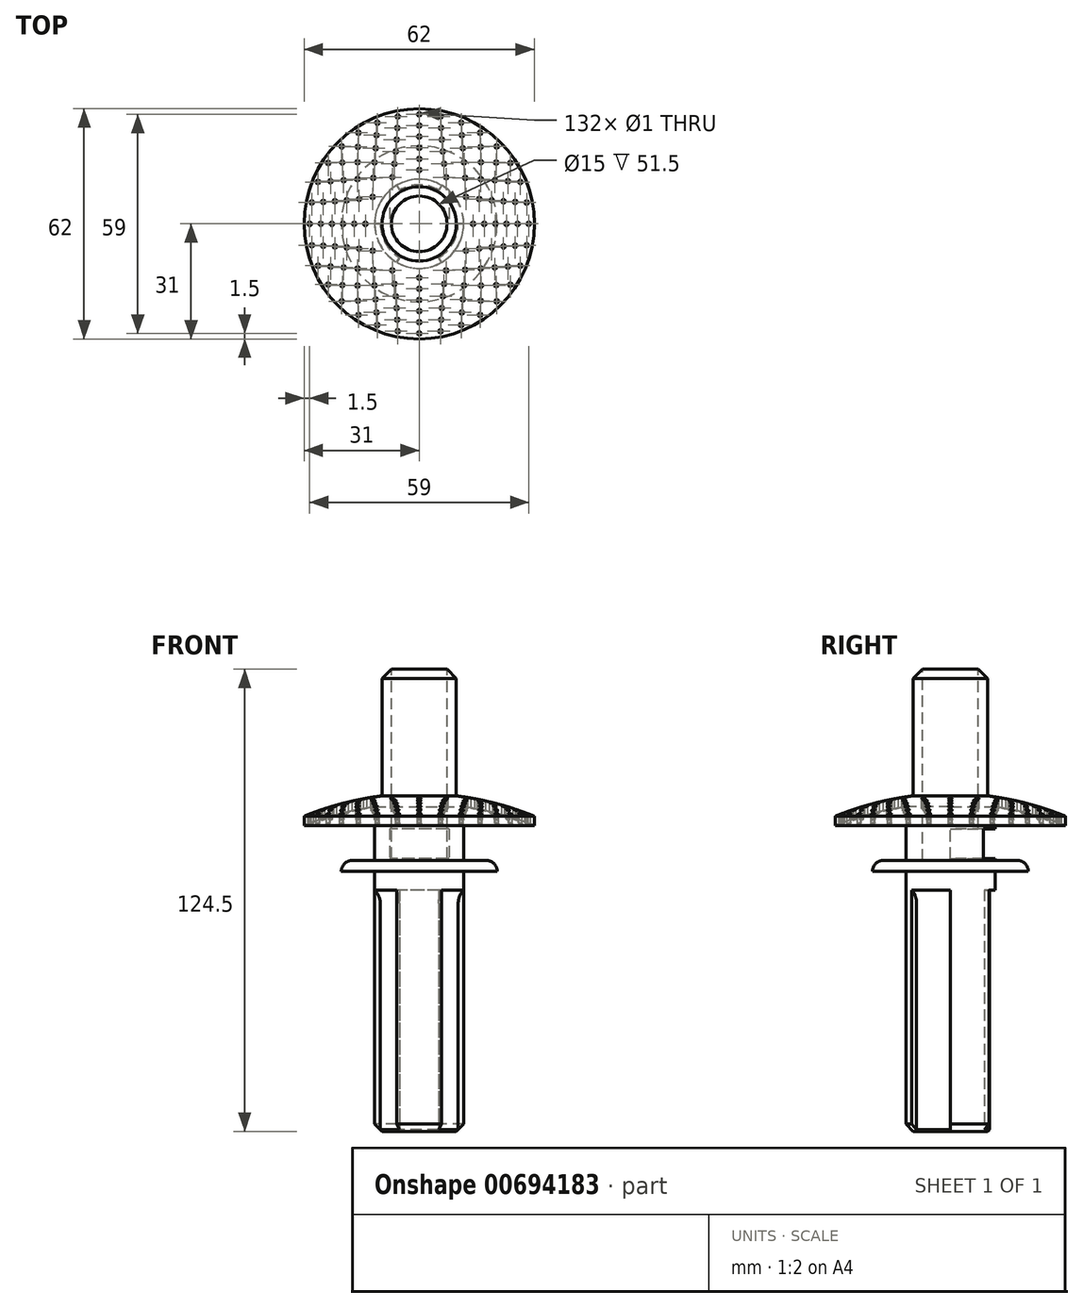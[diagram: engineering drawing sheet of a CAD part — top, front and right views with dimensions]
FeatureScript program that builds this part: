
annotation { "Feature Type Name" : "Feature", "Feature Type Description" : "" }
export const myFeature = defineFeature(function(context is Context, id is Id, definition is map)
    precondition{}
    {
        {
            var Q0;
            Q0=qCreatedBy(makeId("Top.planeOp"),FACE);
            var sketch = newSketch(context, id + "F0", { "sketchPlane" : qUnion([Q0])});
            skArc(sketch, "E0", {"start": v(-6, 10.4) * mm, "mid": v(-10.4, 6) * mm, "end": v(-12, 0) * mm});
            skArc(sketch, "E1", {"start": v(5.25, 9.1) * mm, "mid": v(0, 10.5) * mm, "end": v(-5.25, 9.1) * mm});
            skLineSegment(sketch, "E2", {"start": v(-5.25, 9.1) * mm, "end": v(-6, 10.4) * mm});
            skLineSegment(sketch, "E3", {"start": v(5.25, 9.1) * mm, "end": v(6, 10.4) * mm});
            skArc(sketch, "E4.1.0", {"start": v(-10.5, 0) * mm, "mid": v(-9.1, -5.25) * mm, "end": v(-5.25, -9.1) * mm});
            skArc(sketch, "E4.2.0", {"start": v(5.25, -9.1) * mm, "mid": v(9.1, -5.25) * mm, "end": v(10.5, 0) * mm});
            skLineSegment(sketch, "E5.1.0", {"start": v(-10.5, 0) * mm, "end": v(-12, 0) * mm});
            skLineSegment(sketch, "E5.1.1", {"start": v(-5.25, -9.1) * mm, "end": v(-6, -10.4) * mm});
            skLineSegment(sketch, "E5.2.0", {"start": v(5.25, -9.1) * mm, "end": v(6, -10.4) * mm});
            skLineSegment(sketch, "E5.2.1", {"start": v(10.5, 0) * mm, "end": v(12, 0) * mm});
            skArc(sketch, "E6.trimOffspring", {"start": v(-6, -10.4) * mm, "mid": v(0, -12) * mm, "end": v(6, -10.4) * mm});
            skArc(sketch, "E7.trimOffspring", {"start": v(12, 0) * mm, "mid": v(10.4, 6) * mm, "end": v(6, 10.4) * mm});
            skSolve(sketch);
        }
        {
            var Q0;
            Q0=makeQuery(id+"F0.imprint","IMPRINT",FACE,{"disambiguationData":[TD([[makeQuery(id+"F0.imprint","IMPRINT",EDGE,{"derivedFrom":sQuery(id+"F0.wireOp",EDGE,"E0")}),1.0]])]});
            extrude(context, id + "F1", {"entities" : qUnion([Q0]), "depth" : 65 * mm, "offsetDistance" : 25 * mm});
        }
        {
            var Q0;
            Q0=makeQuery(id+"F1.opExtrude","CAP_FACE",FACE,{"disambiguationData":[OSD([sQuery(id+"F0.wireOp",EDGE,"E0"),sQuery(id+"F0.wireOp",EDGE,"E1"),sQuery(id+"F0.wireOp",EDGE,"E2"),sQuery(id+"F0.wireOp",EDGE,"E3"),sQuery(id+"F0.wireOp",EDGE,"E4.1.0"),sQuery(id+"F0.wireOp",EDGE,"E4.2.0"),sQuery(id+"F0.wireOp",EDGE,"E5.1.0"),sQuery(id+"F0.wireOp",EDGE,"E5.1.1"),sQuery(id+"F0.wireOp",EDGE,"E5.2.0"),sQuery(id+"F0.wireOp",EDGE,"E5.2.1"),sQuery(id+"F0.wireOp",EDGE,"E6.trimOffspring"),sQuery(id+"F0.wireOp",EDGE,"E7.trimOffspring")])],"isStart":false});
            var sketch = newSketch(context, id + "F2", { "sketchPlane" : qUnion([Q0])});
            skCircle(sketch, "E8", {"center": v(0, 0) * mm, "radius": 12 * mm});
            skSolve(sketch);
        }
        {
            var Q0;
            Q0 = qSketchRegion(id + "F2", true);
            extrude(context, id + "F3", {"entities" : qUnion([Q0]), "operationType" : NewBodyOperationType.ADD, "depth" : 25 * mm, "offsetDistance" : 25 * mm});
        }
        {
            var Q0;
            Q0=makeQuery(id+"F1.opExtrude","CAP_EDGE",EDGE,{"disambiguationData":[OSD([sQuery(id+"F0.wireOp",EDGE,"E1")])],"isStart":false});
            var Q1;
            Q1=makeQuery(id+"F1.opExtrude","CAP_EDGE",EDGE,{"disambiguationData":[OSD([sQuery(id+"F0.wireOp",EDGE,"E4.1.0")])],"isStart":false});
            var Q2;
            Q2=makeQuery(id+"F1.opExtrude","CAP_EDGE",EDGE,{"disambiguationData":[OSD([sQuery(id+"F0.wireOp",EDGE,"E4.2.0")])],"isStart":false});
            fillet(context, id + "F4", {"entities" : qUnion([Q0, Q1, Q2]), "radius" : 5 * mm, "tangentPropagation" : true, "allowEdgeOverflow" : false});
        }
        {
            var Q0;
            Q0=makeQuery(id+"F1.opExtrude","CAP_EDGE",EDGE,{"disambiguationData":[OSD([sQuery(id+"F0.wireOp",EDGE,"E6.trimOffspring")])],"isStart":true});
            chamfer(context, id + "F5", {"entities" : qUnion([Q0]), "width" : 2 * mm, "tangentPropagation" : true});
        }
        {
            var Q0;
            Q0=qCreatedBy(makeId("Top.planeOp"),FACE);
            cPlane(context, id + "F6", {"entities" : qUnion([Q0]), "cplaneType" : CPlaneType.OFFSET, "offset" : 70 * mm, "width" : 150 * mm, "height" : 150 * mm});
        }
        {
            var Q0;
            Q0=qCreatedBy(id+"F6.planeOp",FACE);
            var sketch = newSketch(context, id + "F7", { "sketchPlane" : qUnion([Q0])});
            skCircle(sketch, "E9", {"center": v(0, 0) * mm, "radius": 21 * mm});
            skSolve(sketch);
        }
        {
            var Q0;
            Q0 = qSketchRegion(id + "F7", true);
            extrude(context, id + "F8", {"entities" : qUnion([Q0]), "operationType" : NewBodyOperationType.ADD, "depth" : 3 * mm, "offsetDistance" : 25 * mm});
        }
        {
            var Q0;
            Q0=makeQuery(id+"F8.opExtrude","CAP_EDGE",EDGE,{"disambiguationData":[OSD([sQuery(id+"F7.wireOp",EDGE,"E9")])],"isStart":false});
            fillet(context, id + "F9", {"entities" : qUnion([Q0]), "radius" : 3 * mm, "tangentPropagation" : true, "allowEdgeOverflow" : false});
        }
        {
            var Q0;
            Q0=makeQuery(id+"F3.opExtrude","CAP_FACE",FACE,{"disambiguationData":[OSD([sQuery(id+"F2.wireOp",EDGE,"E8")])],"isStart":false});
            var sketch = newSketch(context, id + "F10", { "sketchPlane" : qUnion([Q0])});
            skPoint(sketch, "E10", {"position": v(0, 0) * mm});
            skSolve(sketch);
        }
        {
            var Q0;
            Q0=qCreatedBy(makeId("Front.planeOp"),FACE);
            var sketch = newSketch(context, id + "F11", { "sketchPlane" : qUnion([Q0])});
            skArc(sketch, "E11", {"start": v(0, 90.99) * mm, "mid": v(-15.8, 89.45) * mm, "end": v(-31, 84.9) * mm});
            skLineSegment(sketch, "E12", {"start": v(-31, 84.9) * mm, "end": v(-31, 82.4) * mm});
            skArc(sketch, "E13", {"start": v(0, 88.25) * mm, "mid": v(-15.77, 86.78) * mm, "end": v(-31, 82.4) * mm});
            skLineSegment(sketch, "E14", {"start": v(0, 88.25) * mm, "end": v(0, 90.99) * mm});
            skSolve(sketch);
        }
        {
            var Q0;
            Q0=qCreatedBy(makeId("Front.planeOp"),FACE);
            var sketch = newSketch(context, id + "F12", { "sketchPlane" : qUnion([Q0])});
            skLineSegment(sketch, "E15", {"start": v(0, 0) * mm, "end": v(0, 90) * mm, "construction": true});
            skSolve(sketch);
        }
        {
            var Q0;
            Q0=makeQuery(id+"F11.imprint","IMPRINT",FACE,{"disambiguationData":[TD([[makeQuery(id+"F11.imprint","IMPRINT",EDGE,{"derivedFrom":sQuery(id+"F11.wireOp",EDGE,"E11")}),1.0]])]});
            var Q1;
            Q1=sQuery(id+"F12.wireOp",EDGE,"E15");
            revolve(context, id + "F13", {"operationType" : NewBodyOperationType.ADD, "entities" : qUnion([Q0]), "axis" : qUnion([Q1]), "revolveType" : RevolveType.FULL, "oppositeDirection" : true});
        }
        {
            var Q0;
            Q0=qCreatedBy(id+"F6.planeOp",FACE);
            cPlane(context, id + "F14", {"entities" : qUnion([Q0]), "cplaneType" : CPlaneType.OFFSET, "offset" : 25 * mm, "width" : 150 * mm, "height" : 150 * mm});
        }
        {
            var Q0;
            Q0=qCreatedBy(id+"F14.planeOp",FACE);
            var sketch = newSketch(context, id + "F15", { "sketchPlane" : qUnion([Q0])});
            skCircle(sketch, "E16", {"center": v(0, 14.5) * mm, "radius": 0.5 * mm});
            skLineSegment(sketch, "E17", {"start": v(0, 0) * mm, "end": v(0, 31.17) * mm, "construction": true});
            skCircle(sketch, "E18.0.1.0", {"center": v(0, 17.5) * mm, "radius": 0.5 * mm});
            skCircle(sketch, "E18.0.2.0", {"center": v(0, 20.5) * mm, "radius": 0.5 * mm});
            skCircle(sketch, "E18.0.3.0", {"center": v(0, 23.5) * mm, "radius": 0.5 * mm});
            skLineSegment(sketch, "E18.direction1", {"start": v(0, 14.5) * mm, "end": v(25, 14.5) * mm, "construction": true});
            skLineSegment(sketch, "E18.direction2", {"start": v(0, 14.5) * mm, "end": v(0, 17.5) * mm, "construction": true});
            skCircle(sketch, "E19.0.0.4", {"center": v(0, 26.5) * mm, "radius": 0.5 * mm});
            skCircle(sketch, "E20.0.0.5", {"center": v(0, 29.5) * mm, "radius": 0.5 * mm});
            skPoint(sketch, "E21.center", {"position": v(0, 0) * mm});
            skLineSegment(sketch, "E21.anchor1", {"start": v(0, 0) * mm, "end": v(0, 14.5) * mm, "construction": true});
            skCircle(sketch, "E22.1.0", {"center": v(-7.25, 12.56) * mm, "radius": 0.5 * mm});
            skCircle(sketch, "E22.2.0", {"center": v(-12.56, 7.25) * mm, "radius": 0.5 * mm});
            skCircle(sketch, "E22.3.0", {"center": v(-14.5, 0) * mm, "radius": 0.5 * mm});
            skCircle(sketch, "E22.4.0", {"center": v(-12.56, -7.25) * mm, "radius": 0.5 * mm});
            skCircle(sketch, "E22.5.0", {"center": v(-7.25, -12.56) * mm, "radius": 0.5 * mm});
            skCircle(sketch, "E22.6.0", {"center": v(0, -14.5) * mm, "radius": 0.5 * mm});
            skCircle(sketch, "E22.7.0", {"center": v(7.25, -12.56) * mm, "radius": 0.5 * mm});
            skCircle(sketch, "E22.8.0", {"center": v(12.56, -7.25) * mm, "radius": 0.5 * mm});
            skCircle(sketch, "E22.9.0", {"center": v(14.5, 0) * mm, "radius": 0.5 * mm});
            skCircle(sketch, "E22.10.0", {"center": v(12.56, 7.25) * mm, "radius": 0.5 * mm});
            skCircle(sketch, "E22.11.0", {"center": v(7.25, 12.56) * mm, "radius": 0.5 * mm});
            skCircle(sketch, "E23.1.0", {"center": v(-6.7, 16.17) * mm, "radius": 0.5 * mm});
            skCircle(sketch, "E23.2.0", {"center": v(-12.37, 12.37) * mm, "radius": 0.5 * mm});
            skCircle(sketch, "E23.3.0", {"center": v(-16.17, 6.7) * mm, "radius": 0.5 * mm});
            skCircle(sketch, "E23.4.0", {"center": v(-17.5, 0) * mm, "radius": 0.5 * mm});
            skCircle(sketch, "E23.5.0", {"center": v(-16.17, -6.7) * mm, "radius": 0.5 * mm});
            skCircle(sketch, "E23.6.0", {"center": v(-12.37, -12.37) * mm, "radius": 0.5 * mm});
            skCircle(sketch, "E23.7.0", {"center": v(-6.7, -16.17) * mm, "radius": 0.5 * mm});
            skCircle(sketch, "E23.8.0", {"center": v(0, -17.5) * mm, "radius": 0.5 * mm});
            skCircle(sketch, "E23.9.0", {"center": v(6.7, -16.17) * mm, "radius": 0.5 * mm});
            skCircle(sketch, "E23.10.0", {"center": v(12.37, -12.37) * mm, "radius": 0.5 * mm});
            skCircle(sketch, "E23.11.0", {"center": v(16.17, -6.7) * mm, "radius": 0.5 * mm});
            skCircle(sketch, "E23.12.0", {"center": v(17.5, 0) * mm, "radius": 0.5 * mm});
            skCircle(sketch, "E23.13.0", {"center": v(16.17, 6.7) * mm, "radius": 0.5 * mm});
            skCircle(sketch, "E23.14.0", {"center": v(12.37, 12.37) * mm, "radius": 0.5 * mm});
            skCircle(sketch, "E23.15.0", {"center": v(6.7, 16.17) * mm, "radius": 0.5 * mm});
            skCircle(sketch, "E24.1.0", {"center": v(-6.33, 19.5) * mm, "radius": 0.5 * mm});
            skCircle(sketch, "E24.2.0", {"center": v(-12.05, 16.58) * mm, "radius": 0.5 * mm});
            skCircle(sketch, "E24.3.0", {"center": v(-16.58, 12.05) * mm, "radius": 0.5 * mm});
            skCircle(sketch, "E24.4.0", {"center": v(-19.5, 6.33) * mm, "radius": 0.5 * mm});
            skCircle(sketch, "E24.5.0", {"center": v(-20.5, 0) * mm, "radius": 0.5 * mm});
            skCircle(sketch, "E24.6.0", {"center": v(-19.5, -6.33) * mm, "radius": 0.5 * mm});
            skCircle(sketch, "E24.7.0", {"center": v(-16.58, -12.05) * mm, "radius": 0.5 * mm});
            skCircle(sketch, "E24.8.0", {"center": v(-12.05, -16.58) * mm, "radius": 0.5 * mm});
            skCircle(sketch, "E24.9.0", {"center": v(-6.33, -19.5) * mm, "radius": 0.5 * mm});
            skCircle(sketch, "E24.10.0", {"center": v(0, -20.5) * mm, "radius": 0.5 * mm});
            skCircle(sketch, "E24.11.0", {"center": v(6.33, -19.5) * mm, "radius": 0.5 * mm});
            skCircle(sketch, "E24.12.0", {"center": v(12.05, -16.58) * mm, "radius": 0.5 * mm});
            skCircle(sketch, "E24.13.0", {"center": v(16.58, -12.05) * mm, "radius": 0.5 * mm});
            skCircle(sketch, "E24.14.0", {"center": v(19.5, -6.33) * mm, "radius": 0.5 * mm});
            skCircle(sketch, "E24.15.0", {"center": v(20.5, 0) * mm, "radius": 0.5 * mm});
            skCircle(sketch, "E24.16.0", {"center": v(19.5, 6.33) * mm, "radius": 0.5 * mm});
            skCircle(sketch, "E24.17.0", {"center": v(16.58, 12.05) * mm, "radius": 0.5 * mm});
            skCircle(sketch, "E24.18.0", {"center": v(12.05, 16.58) * mm, "radius": 0.5 * mm});
            skCircle(sketch, "E24.19.0", {"center": v(6.33, 19.5) * mm, "radius": 0.5 * mm});
            skCircle(sketch, "E25.1.0", {"center": v(-6.08, 22.7) * mm, "radius": 0.5 * mm});
            skCircle(sketch, "E25.2.0", {"center": v(-11.75, 20.35) * mm, "radius": 0.5 * mm});
            skCircle(sketch, "E25.3.0", {"center": v(-16.62, 16.62) * mm, "radius": 0.5 * mm});
            skCircle(sketch, "E25.4.0", {"center": v(-20.35, 11.75) * mm, "radius": 0.5 * mm});
            skCircle(sketch, "E25.5.0", {"center": v(-22.7, 6.08) * mm, "radius": 0.5 * mm});
            skCircle(sketch, "E25.6.0", {"center": v(-23.5, 0) * mm, "radius": 0.5 * mm});
            skCircle(sketch, "E25.7.0", {"center": v(-22.7, -6.08) * mm, "radius": 0.5 * mm});
            skCircle(sketch, "E25.8.0", {"center": v(-20.35, -11.75) * mm, "radius": 0.5 * mm});
            skCircle(sketch, "E25.9.0", {"center": v(-16.62, -16.62) * mm, "radius": 0.5 * mm});
            skCircle(sketch, "E25.10.0", {"center": v(-11.75, -20.35) * mm, "radius": 0.5 * mm});
            skCircle(sketch, "E25.11.0", {"center": v(-6.08, -22.7) * mm, "radius": 0.5 * mm});
            skCircle(sketch, "E25.12.0", {"center": v(0, -23.5) * mm, "radius": 0.5 * mm});
            skCircle(sketch, "E25.13.0", {"center": v(6.08, -22.7) * mm, "radius": 0.5 * mm});
            skCircle(sketch, "E25.14.0", {"center": v(11.75, -20.35) * mm, "radius": 0.5 * mm});
            skCircle(sketch, "E25.15.0", {"center": v(16.62, -16.62) * mm, "radius": 0.5 * mm});
            skCircle(sketch, "E25.16.0", {"center": v(20.35, -11.75) * mm, "radius": 0.5 * mm});
            skCircle(sketch, "E25.17.0", {"center": v(22.7, -6.08) * mm, "radius": 0.5 * mm});
            skCircle(sketch, "E25.18.0", {"center": v(23.5, 0) * mm, "radius": 0.5 * mm});
            skCircle(sketch, "E25.19.0", {"center": v(22.7, 6.08) * mm, "radius": 0.5 * mm});
            skCircle(sketch, "E25.20.0", {"center": v(20.35, 11.75) * mm, "radius": 0.5 * mm});
            skCircle(sketch, "E25.21.0", {"center": v(16.62, 16.62) * mm, "radius": 0.5 * mm});
            skCircle(sketch, "E25.22.0", {"center": v(11.75, 20.35) * mm, "radius": 0.5 * mm});
            skCircle(sketch, "E25.23.0", {"center": v(6.08, 22.7) * mm, "radius": 0.5 * mm});
            skCircle(sketch, "E26.1.0", {"center": v(-5.9, 25.84) * mm, "radius": 0.5 * mm});
            skCircle(sketch, "E26.2.0", {"center": v(-11.5, 23.88) * mm, "radius": 0.5 * mm});
            skCircle(sketch, "E26.3.0", {"center": v(-16.52, 20.72) * mm, "radius": 0.5 * mm});
            skCircle(sketch, "E26.4.0", {"center": v(-20.72, 16.52) * mm, "radius": 0.5 * mm});
            skCircle(sketch, "E26.5.0", {"center": v(-23.88, 11.5) * mm, "radius": 0.5 * mm});
            skCircle(sketch, "E26.6.0", {"center": v(-25.84, 5.9) * mm, "radius": 0.5 * mm});
            skCircle(sketch, "E26.7.0", {"center": v(-26.5, 0) * mm, "radius": 0.5 * mm});
            skCircle(sketch, "E26.8.0", {"center": v(-25.84, -5.9) * mm, "radius": 0.5 * mm});
            skCircle(sketch, "E26.9.0", {"center": v(-23.88, -11.5) * mm, "radius": 0.5 * mm});
            skCircle(sketch, "E26.10.0", {"center": v(-20.72, -16.52) * mm, "radius": 0.5 * mm});
            skCircle(sketch, "E26.11.0", {"center": v(-16.52, -20.72) * mm, "radius": 0.5 * mm});
            skCircle(sketch, "E26.12.0", {"center": v(-11.5, -23.88) * mm, "radius": 0.5 * mm});
            skCircle(sketch, "E26.13.0", {"center": v(-5.9, -25.84) * mm, "radius": 0.5 * mm});
            skCircle(sketch, "E26.14.0", {"center": v(0, -26.5) * mm, "radius": 0.5 * mm});
            skCircle(sketch, "E26.15.0", {"center": v(5.9, -25.84) * mm, "radius": 0.5 * mm});
            skCircle(sketch, "E26.16.0", {"center": v(11.5, -23.88) * mm, "radius": 0.5 * mm});
            skCircle(sketch, "E26.17.0", {"center": v(16.52, -20.72) * mm, "radius": 0.5 * mm});
            skCircle(sketch, "E26.18.0", {"center": v(20.72, -16.52) * mm, "radius": 0.5 * mm});
            skCircle(sketch, "E26.19.0", {"center": v(23.88, -11.5) * mm, "radius": 0.5 * mm});
            skCircle(sketch, "E26.20.0", {"center": v(25.84, -5.9) * mm, "radius": 0.5 * mm});
            skCircle(sketch, "E26.21.0", {"center": v(26.5, 0) * mm, "radius": 0.5 * mm});
            skCircle(sketch, "E26.22.0", {"center": v(25.84, 5.9) * mm, "radius": 0.5 * mm});
            skCircle(sketch, "E26.23.0", {"center": v(23.88, 11.5) * mm, "radius": 0.5 * mm});
            skCircle(sketch, "E26.24.0", {"center": v(20.72, 16.52) * mm, "radius": 0.5 * mm});
            skCircle(sketch, "E26.25.0", {"center": v(16.52, 20.72) * mm, "radius": 0.5 * mm});
            skCircle(sketch, "E26.26.0", {"center": v(11.5, 23.88) * mm, "radius": 0.5 * mm});
            skCircle(sketch, "E26.27.0", {"center": v(5.9, 25.84) * mm, "radius": 0.5 * mm});
            skCircle(sketch, "E27.1.0", {"center": v(-5.76, 28.93) * mm, "radius": 0.5 * mm});
            skCircle(sketch, "E27.2.0", {"center": v(-11.29, 27.25) * mm, "radius": 0.5 * mm});
            skCircle(sketch, "E27.3.0", {"center": v(-16.39, 24.53) * mm, "radius": 0.5 * mm});
            skCircle(sketch, "E27.4.0", {"center": v(-20.86, 20.86) * mm, "radius": 0.5 * mm});
            skCircle(sketch, "E27.5.0", {"center": v(-24.53, 16.39) * mm, "radius": 0.5 * mm});
            skCircle(sketch, "E27.6.0", {"center": v(-27.25, 11.29) * mm, "radius": 0.5 * mm});
            skCircle(sketch, "E27.7.0", {"center": v(-28.93, 5.76) * mm, "radius": 0.5 * mm});
            skCircle(sketch, "E27.8.0", {"center": v(-29.5, 0) * mm, "radius": 0.5 * mm});
            skCircle(sketch, "E27.9.0", {"center": v(-28.93, -5.76) * mm, "radius": 0.5 * mm});
            skCircle(sketch, "E27.10.0", {"center": v(-27.25, -11.29) * mm, "radius": 0.5 * mm});
            skCircle(sketch, "E27.11.0", {"center": v(-24.53, -16.39) * mm, "radius": 0.5 * mm});
            skCircle(sketch, "E27.12.0", {"center": v(-20.86, -20.86) * mm, "radius": 0.5 * mm});
            skCircle(sketch, "E27.13.0", {"center": v(-16.39, -24.53) * mm, "radius": 0.5 * mm});
            skCircle(sketch, "E27.14.0", {"center": v(-11.29, -27.25) * mm, "radius": 0.5 * mm});
            skCircle(sketch, "E27.15.0", {"center": v(-5.76, -28.93) * mm, "radius": 0.5 * mm});
            skCircle(sketch, "E27.16.0", {"center": v(0, -29.5) * mm, "radius": 0.5 * mm});
            skCircle(sketch, "E27.17.0", {"center": v(5.76, -28.93) * mm, "radius": 0.5 * mm});
            skCircle(sketch, "E27.18.0", {"center": v(11.29, -27.25) * mm, "radius": 0.5 * mm});
            skCircle(sketch, "E27.19.0", {"center": v(16.39, -24.53) * mm, "radius": 0.5 * mm});
            skCircle(sketch, "E27.20.0", {"center": v(20.86, -20.86) * mm, "radius": 0.5 * mm});
            skCircle(sketch, "E27.21.0", {"center": v(24.53, -16.39) * mm, "radius": 0.5 * mm});
            skCircle(sketch, "E27.22.0", {"center": v(27.25, -11.29) * mm, "radius": 0.5 * mm});
            skCircle(sketch, "E27.23.0", {"center": v(28.93, -5.76) * mm, "radius": 0.5 * mm});
            skCircle(sketch, "E27.24.0", {"center": v(29.5, 0) * mm, "radius": 0.5 * mm});
            skCircle(sketch, "E27.25.0", {"center": v(28.93, 5.76) * mm, "radius": 0.5 * mm});
            skCircle(sketch, "E27.26.0", {"center": v(27.25, 11.29) * mm, "radius": 0.5 * mm});
            skCircle(sketch, "E27.27.0", {"center": v(24.53, 16.39) * mm, "radius": 0.5 * mm});
            skCircle(sketch, "E27.28.0", {"center": v(20.86, 20.86) * mm, "radius": 0.5 * mm});
            skCircle(sketch, "E27.29.0", {"center": v(16.39, 24.53) * mm, "radius": 0.5 * mm});
            skCircle(sketch, "E27.30.0", {"center": v(11.29, 27.25) * mm, "radius": 0.5 * mm});
            skCircle(sketch, "E27.31.0", {"center": v(5.76, 28.93) * mm, "radius": 0.5 * mm});
            skSolve(sketch);
        }
        {
            var Q0;
            Q0 = qSketchRegion(id + "F15", true);
            extrude(context, id + "F16", {"entities" : qUnion([Q0]), "operationType" : NewBodyOperationType.REMOVE, "oppositeDirection" : true, "depth" : 15 * mm, "offsetDistance" : 25 * mm});
        }
        {
            var Q0;
            Q0=qCreatedBy(id+"F14.planeOp",FACE);
            cPlane(context, id + "F17", {"entities" : qUnion([Q0]), "cplaneType" : CPlaneType.OFFSET, "offset" : 5 * mm, "oppositeDirection" : true, "width" : 150 * mm, "height" : 150 * mm});
        }
        {
            var Q0;
            Q0=qCreatedBy(id+"F17.planeOp",FACE);
            var sketch = newSketch(context, id + "F18", { "sketchPlane" : qUnion([Q0])});
            skCircle(sketch, "E28", {"center": v(0, 0) * mm, "radius": 10 * mm});
            skSolve(sketch);
        }
        {
            var Q0;
            Q0 = qSketchRegion(id + "F18", true);
            var Q1;
            Q1=sQuery(id+"F18.wireOp",EDGE,"E28");
            extrude(context, id + "F19", {"entities" : qUnion([Q0]), "operationType" : NewBodyOperationType.ADD, "surfaceEntities" : qUnion([Q1]), "depth" : 35 * mm, "offsetDistance" : 25 * mm});
        }
        {
            var Q0;
            Q0=makeQuery(id+"F19.opExtrude","CAP_EDGE",EDGE,{"disambiguationData":[OSD([sQuery(id+"F18.wireOp",EDGE,"E28")])],"isStart":false});
            chamfer(context, id + "F20", {"entities" : qUnion([Q0]), "width" : 3 * mm, "tangentPropagation" : true});
        }
        {
            var Q0;
            Q0=qCreatedBy(makeId("Front.planeOp"),FACE);
            var sketch = newSketch(context, id + "F21", { "sketchPlane" : qUnion([Q0])});
            skLineSegment(sketch, "E29.bottom", {"start": v(8, 81.5) * mm, "end": v(-8, 81.5) * mm});
            skLineSegment(sketch, "E29.top", {"start": v(8, 73.5) * mm, "end": v(-8, 73.5) * mm});
            skLineSegment(sketch, "E29.left", {"start": v(8, 81.5) * mm, "end": v(8, 73.5) * mm});
            skLineSegment(sketch, "E29.right", {"start": v(-8, 81.5) * mm, "end": v(-8, 73.5) * mm});
            skSolve(sketch);
        }
        {
            var Q0;
            Q0 = qSketchRegion(id + "F21", true);
            extrude(context, id + "F22", {"entities" : qUnion([Q0]), "operationType" : NewBodyOperationType.REMOVE, "oppositeDirection" : true, "depth" : 25 * mm, "offsetDistance" : 25 * mm});
        }
        {
            var Q0;
            Q0=makeQuery(id+"F19.opExtrude","CAP_FACE",FACE,{"disambiguationData":[OSD([sQuery(id+"F18.wireOp",EDGE,"E28")])],"isStart":false});
            var sketch = newSketch(context, id + "F23", { "sketchPlane" : qUnion([Q0])});
            skCircle(sketch, "E30", {"center": v(0, 0) * mm, "radius": 7.5 * mm});
            skSolve(sketch);
        }
        {
            var Q0;
            Q0 = qSketchRegion(id + "F23", true);
            extrude(context, id + "F24", {"entities" : qUnion([Q0]), "operationType" : NewBodyOperationType.REMOVE, "oppositeDirection" : true, "depth" : 52 * mm, "offsetDistance" : 25 * mm});
        }
    });
